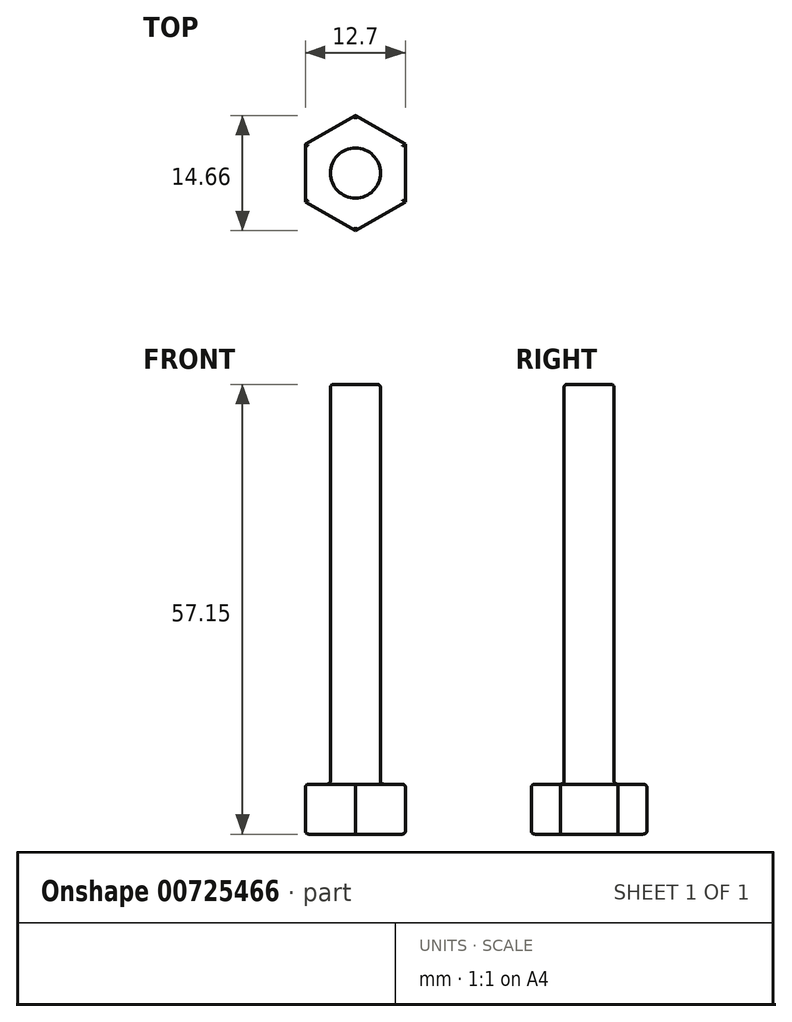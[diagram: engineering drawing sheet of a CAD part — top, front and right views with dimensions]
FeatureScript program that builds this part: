
annotation { "Feature Type Name" : "Feature", "Feature Type Description" : "" }
export const myFeature = defineFeature(function(context is Context, id is Id, definition is map)
    precondition{}
    {
        {
            var Q0;
            Q0=qCreatedBy(makeId("Top.planeOp"),FACE);
            var sketch = newSketch(context, id + "F0", { "sketchPlane" : qUnion([Q0])});
            skCircle(sketch, "E0", {"center": v(0, 0) * mm, "radius": 3.17 * mm});
            skCircle(sketch, "E1.cCircle", {"center": v(0, 0) * mm, "radius": 6.35 * mm, "construction": true});
            skLineSegment(sketch, "E1.0", {"start": v(6.35, 3.67) * mm, "end": v(6.35, -3.67) * mm});
            skLineSegment(sketch, "E1.1", {"start": v(6.35, -3.67) * mm, "end": v(0, -7.33) * mm});
            skLineSegment(sketch, "E1.2", {"start": v(0, -7.33) * mm, "end": v(-6.35, -3.67) * mm});
            skLineSegment(sketch, "E1.3", {"start": v(-6.35, -3.67) * mm, "end": v(-6.35, 3.67) * mm});
            skLineSegment(sketch, "E1.4", {"start": v(-6.35, 3.67) * mm, "end": v(0, 7.33) * mm});
            skLineSegment(sketch, "E1.5", {"start": v(0, 7.33) * mm, "end": v(6.35, 3.67) * mm});
            skPoint(sketch, "E1.0.midPoint", {"position": v(6.35, 0) * mm});
            skSolve(sketch);
        }
        {
            var Q0;
            Q0=makeQuery(id+"F0.imprint","IMPRINT",FACE,{"disambiguationData":[TD([[makeQuery(id+"F0.imprint","IMPRINT",EDGE,{"derivedFrom":sQuery(id+"F0.wireOp",EDGE,"E0")}),1.0]])]});
            extrude(context, id + "F1", {"entities" : qUnion([Q0]), "depth" : 57.15 * mm, "offsetDistance" : 25.4 * mm});
        }
        {
            var Q0;
            Q0=makeQuery(id+"F0.imprint","IMPRINT",FACE,{"disambiguationData":[TD([[makeQuery(id+"F0.imprint","IMPRINT",EDGE,{"derivedFrom":sQuery(id+"F0.wireOp",EDGE,"E0")}),-1.0]])]});
            extrude(context, id + "F2", {"entities" : qUnion([Q0]), "operationType" : NewBodyOperationType.ADD, "depth" : 6.35 * mm, "offsetDistance" : 25.4 * mm});
        }
        {
            var Q0;
            Q0=makeQuery(id+"F2.opExtrude","CAP_FACE",FACE,{"disambiguationData":[OSD([sQuery(id+"F0.wireOp",EDGE,"E0"),sQuery(id+"F0.wireOp",EDGE,"E1.0"),sQuery(id+"F0.wireOp",EDGE,"E1.1"),sQuery(id+"F0.wireOp",EDGE,"E1.2"),sQuery(id+"F0.wireOp",EDGE,"E1.3"),sQuery(id+"F0.wireOp",EDGE,"E1.4"),sQuery(id+"F0.wireOp",EDGE,"E1.5")])],"isStart":false});
            var Q1;
            {var subQ0=sQuery(id+"F0.wireOp",EDGE,"E0");Q1=makeQuery(id+"F2.boolean.opBoolean","MERGE",FACE,{"derivedFrom":[makeQuery(id+"F1.opExtrude","CAP_FACE",FACE,{"disambiguationData":[OSD([subQ0])],"isStart":true}),makeQuery(id+"F2.opExtrude","CAP_FACE",FACE,{"disambiguationData":[OSD([subQ0,sQuery(id+"F0.wireOp",EDGE,"E1.0"),sQuery(id+"F0.wireOp",EDGE,"E1.1"),sQuery(id+"F0.wireOp",EDGE,"E1.2"),sQuery(id+"F0.wireOp",EDGE,"E1.3"),sQuery(id+"F0.wireOp",EDGE,"E1.4"),sQuery(id+"F0.wireOp",EDGE,"E1.5")])],"isStart":true})]});}
            var Q2;
            Q2=makeQuery(id+"F1.opExtrude","CAP_FACE",FACE,{"disambiguationData":[OSD([sQuery(id+"F0.wireOp",EDGE,"E0")])],"isStart":false});
            fillet(context, id + "F3", {"entities" : qUnion([Q0, Q1, Q2]), "radius" : 0.4 * mm, "tangentPropagation" : true, "allowEdgeOverflow" : false});
        }
    });
